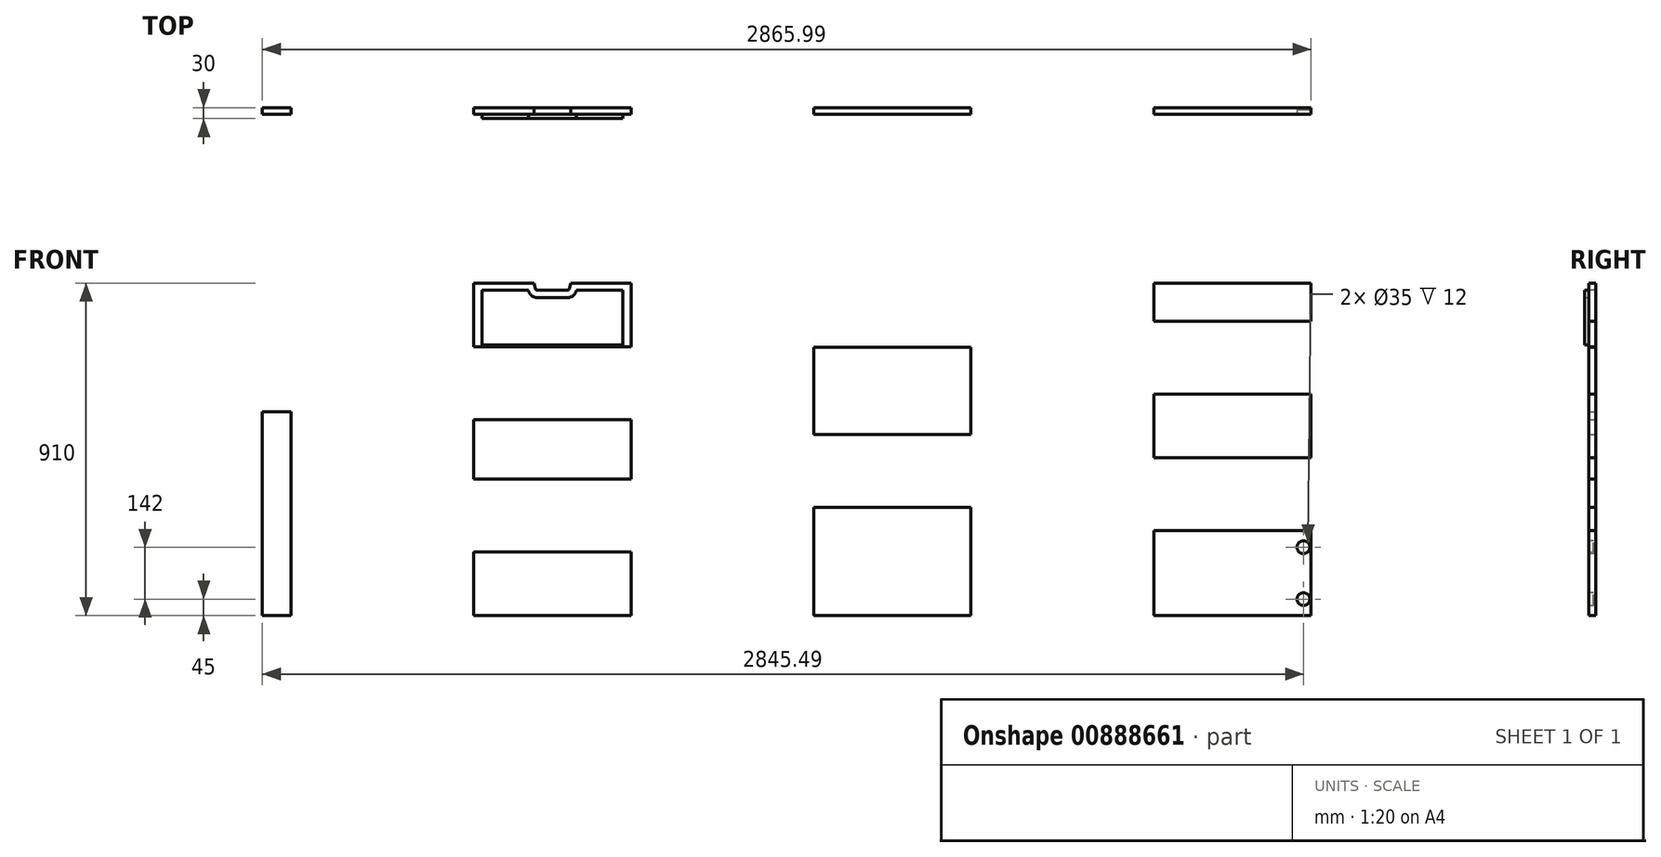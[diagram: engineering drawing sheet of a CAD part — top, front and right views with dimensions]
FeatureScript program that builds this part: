
annotation { "Feature Type Name" : "Feature", "Feature Type Description" : "" }
export const myFeature = defineFeature(function(context is Context, id is Id, definition is map)
    precondition{}
    {
        {
            assignVariable(context, id + "F0", {"name" : "ply", "anyValue" : 18});
        }
        {
            var Q0;
            Q0=qCreatedBy(makeId("Front.planeOp"),FACE);
            var sketch = newSketch(context, id + "F1", { "sketchPlane" : qUnion([Q0])});
            skLineSegment(sketch, "E0.bottom", {"start": v(0, 0) * mm, "end": v(429.33, 0) * mm});
            skLineSegment(sketch, "E0.top", {"start": v(0, 174) * mm, "end": v(429.33, 174) * mm});
            skLineSegment(sketch, "E0.left", {"start": v(0, 0) * mm, "end": v(0, 174) * mm});
            skLineSegment(sketch, "E0.right", {"start": v(429.33, 0) * mm, "end": v(429.33, 174) * mm});
            skLineSegment(sketch, "E1.bottom", {"start": v(0, -362) * mm, "end": v(429.33, -362) * mm});
            skLineSegment(sketch, "E1.top", {"start": v(0, -200) * mm, "end": v(429.33, -200) * mm});
            skLineSegment(sketch, "E1.left", {"start": v(0, -362) * mm, "end": v(0, -200) * mm});
            skLineSegment(sketch, "E1.right", {"start": v(429.33, -362) * mm, "end": v(429.33, -200) * mm});
            skLineSegment(sketch, "E2.bottom", {"start": v(0, -736) * mm, "end": v(429.33, -736) * mm});
            skLineSegment(sketch, "E2.top", {"start": v(0, -562) * mm, "end": v(429.33, -562) * mm});
            skLineSegment(sketch, "E2.left", {"start": v(0, -736) * mm, "end": v(0, -562) * mm});
            skLineSegment(sketch, "E2.right", {"start": v(429.33, -736) * mm, "end": v(429.33, -562) * mm});
            skLineSegment(sketch, "E3.bottom", {"start": v(-578, -736) * mm, "end": v(-500, -736) * mm});
            skLineSegment(sketch, "E3.top", {"start": v(-578, -178) * mm, "end": v(-500, -178) * mm});
            skLineSegment(sketch, "E3.left", {"start": v(-578, -736) * mm, "end": v(-578, -178) * mm});
            skLineSegment(sketch, "E3.right", {"start": v(-500, -736) * mm, "end": v(-500, -178) * mm});
            skLineSegment(sketch, "E4.bottom", {"start": v(929.33, -736) * mm, "end": v(1358.66, -736) * mm});
            skLineSegment(sketch, "E4.top", {"start": v(929.33, -440) * mm, "end": v(1358.66, -440) * mm});
            skLineSegment(sketch, "E4.left", {"start": v(929.33, -736) * mm, "end": v(929.33, -440) * mm});
            skLineSegment(sketch, "E4.right", {"start": v(1358.66, -736) * mm, "end": v(1358.66, -440) * mm});
            skLineSegment(sketch, "E5.bottom", {"start": v(929.33, -240) * mm, "end": v(1358.66, -240) * mm});
            skLineSegment(sketch, "E5.top", {"start": v(929.33, -2) * mm, "end": v(1358.66, -2) * mm});
            skLineSegment(sketch, "E5.left", {"start": v(929.33, -240) * mm, "end": v(929.33, -2) * mm});
            skLineSegment(sketch, "E5.right", {"start": v(1358.66, -240) * mm, "end": v(1358.66, -2) * mm});
            skLineSegment(sketch, "E6.bottom", {"start": v(1858.66, -736) * mm, "end": v(2287.99, -736) * mm});
            skLineSegment(sketch, "E6.top", {"start": v(1858.66, -504) * mm, "end": v(2287.99, -504) * mm});
            skLineSegment(sketch, "E6.left", {"start": v(1858.66, -736) * mm, "end": v(1858.66, -504) * mm});
            skLineSegment(sketch, "E6.right", {"start": v(2287.99, -736) * mm, "end": v(2287.99, -504) * mm});
            skLineSegment(sketch, "E7.bottom", {"start": v(1858.66, -304) * mm, "end": v(2287.99, -304) * mm});
            skLineSegment(sketch, "E7.top", {"start": v(1858.66, -130) * mm, "end": v(2287.99, -130) * mm});
            skLineSegment(sketch, "E7.left", {"start": v(1858.66, -304) * mm, "end": v(1858.66, -130) * mm});
            skLineSegment(sketch, "E7.right", {"start": v(2287.99, -304) * mm, "end": v(2287.99, -130) * mm});
            skLineSegment(sketch, "E8.bottom", {"start": v(1858.66, 70) * mm, "end": v(2287.99, 70) * mm});
            skLineSegment(sketch, "E8.top", {"start": v(1858.66, 174) * mm, "end": v(2287.99, 174) * mm});
            skLineSegment(sketch, "E8.left", {"start": v(1858.66, 70) * mm, "end": v(1858.66, 174) * mm});
            skLineSegment(sketch, "E8.right", {"start": v(2287.99, 70) * mm, "end": v(2287.99, 174) * mm});
            skSolve(sketch);
        }
        {
            var Q0;
            Q0=makeQuery(id+"F1.imprint","IMPRINT",FACE,{"disambiguationData":[TD([[makeQuery(id+"F1.imprint","IMPRINT",EDGE,{"derivedFrom":sQuery(id+"F1.wireOp",EDGE,"E3.bottom")}),1.0]])]});
            var Q1;
            Q1=makeQuery(id+"F1.imprint","IMPRINT",FACE,{"disambiguationData":[TD([[makeQuery(id+"F1.imprint","IMPRINT",EDGE,{"derivedFrom":sQuery(id+"F1.wireOp",EDGE,"E0.bottom")}),1.0]])]});
            var Q2;
            Q2=makeQuery(id+"F1.imprint","IMPRINT",FACE,{"disambiguationData":[TD([[makeQuery(id+"F1.imprint","IMPRINT",EDGE,{"derivedFrom":sQuery(id+"F1.wireOp",EDGE,"E1.bottom")}),1.0]])]});
            var Q3;
            Q3=makeQuery(id+"F1.imprint","IMPRINT",FACE,{"disambiguationData":[TD([[makeQuery(id+"F1.imprint","IMPRINT",EDGE,{"derivedFrom":sQuery(id+"F1.wireOp",EDGE,"E2.bottom")}),1.0]])]});
            var Q4;
            Q4=makeQuery(id+"F1.imprint","IMPRINT",FACE,{"disambiguationData":[TD([[makeQuery(id+"F1.imprint","IMPRINT",EDGE,{"derivedFrom":sQuery(id+"F1.wireOp",EDGE,"E5.bottom")}),1.0]])]});
            var Q5;
            Q5=makeQuery(id+"F1.imprint","IMPRINT",FACE,{"disambiguationData":[TD([[makeQuery(id+"F1.imprint","IMPRINT",EDGE,{"derivedFrom":sQuery(id+"F1.wireOp",EDGE,"E4.bottom")}),1.0]])]});
            var Q6;
            Q6=makeQuery(id+"F1.imprint","IMPRINT",FACE,{"disambiguationData":[TD([[makeQuery(id+"F1.imprint","IMPRINT",EDGE,{"derivedFrom":sQuery(id+"F1.wireOp",EDGE,"E8.bottom")}),1.0]])]});
            var Q7;
            Q7=makeQuery(id+"F1.imprint","IMPRINT",FACE,{"disambiguationData":[TD([[makeQuery(id+"F1.imprint","IMPRINT",EDGE,{"derivedFrom":sQuery(id+"F1.wireOp",EDGE,"E7.bottom")}),1.0]])]});
            var Q8;
            Q8=makeQuery(id+"F1.imprint","IMPRINT",FACE,{"disambiguationData":[TD([[makeQuery(id+"F1.imprint","IMPRINT",EDGE,{"derivedFrom":sQuery(id+"F1.wireOp",EDGE,"E6.bottom")}),1.0]])]});
            extrude(context, id + "F2", {"entities" : qUnion([Q0, Q1, Q2, Q3, Q4, Q5, Q6, Q7, Q8]), "depth" : (getVariable(context, 'ply')) * mm, "offsetDistance" : 25 * mm});
        }
        {
            var Q0;
            Q0=makeQuery(id+"F2.opExtrude","CAP_FACE",FACE,{"disambiguationData":[OSD([sQuery(id+"F1.wireOp",EDGE,"E6.bottom"),sQuery(id+"F1.wireOp",EDGE,"E6.top"),sQuery(id+"F1.wireOp",EDGE,"E6.left"),sQuery(id+"F1.wireOp",EDGE,"E6.right")])],"isStart":false});
            var sketch = newSketch(context, id + "F3", { "sketchPlane" : qUnion([Q0])});
            skCircle(sketch, "E9", {"center": v(2267.49, -549) * mm, "radius": 17.5 * mm});
            skLineSegment(sketch, "E10", {"start": v(1858.66, -620) * mm, "end": v(2287.99, -620) * mm, "construction": true});
            skCircle(sketch, "E11.MirrorC", {"center": v(2267.49, -691) * mm, "radius": 17.5 * mm});
            skSolve(sketch);
        }
        {
            var Q0;
            Q0 = qSketchRegion(id + "F3", true);
            extrude(context, id + "F4", {"entities" : qUnion([Q0]), "operationType" : NewBodyOperationType.REMOVE, "oppositeDirection" : true, "depth" : 12 * mm, "offsetDistance" : 25 * mm});
        }
        {
            var Q0;
            Q0=makeQuery(id+"F2.opExtrude","CAP_FACE",FACE,{"disambiguationData":[OSD([sQuery(id+"F1.wireOp",EDGE,"E0.bottom"),sQuery(id+"F1.wireOp",EDGE,"E0.top"),sQuery(id+"F1.wireOp",EDGE,"E0.left"),sQuery(id+"F1.wireOp",EDGE,"E0.right")])],"isStart":false});
            var sketch = newSketch(context, id + "F5", { "sketchPlane" : qUnion([Q0])});
            skLineSegment(sketch, "E12", {"start": v(214.66, 174) * mm, "end": v(214.66, 0) * mm, "construction": true});
            skLineSegment(sketch, "E13.0", {"start": v(173.5, 154) * mm, "end": v(214.66, 154) * mm});
            skLineSegment(sketch, "E14", {"start": v(168.67, 157.7) * mm, "end": v(164.3, 174) * mm});
            skPoint(sketch, "E15.visualSharp", {"position": v(169.67, 154) * mm});
            skArc(sketch, "E15.filletArc", {"start": v(168.67, 157.7) * mm, "mid": v(170.46, 155.03) * mm, "end": v(173.5, 154) * mm});
            skArc(sketch, "E16.MirrorCS", {"start": v(260.66, 157.7) * mm, "mid": v(258.87, 155.03) * mm, "end": v(255.83, 154) * mm});
            skLineSegment(sketch, "E17.MirrorCS", {"start": v(255.83, 154) * mm, "end": v(214.66, 154) * mm});
            skLineSegment(sketch, "E18.MirrorCS", {"start": v(260.66, 157.7) * mm, "end": v(265.02, 174) * mm});
            skSolve(sketch);
        }
        {
            var Q0;
            Q0=makeQuery(id+"F5.imprint","IMPRINT",FACE,{"disambiguationData":[TD([[makeQuery(id+"F5.imprint","IMPRINT",EDGE,{"derivedFrom":sQuery(id+"F5.wireOp",EDGE,"E13.0")}),1.0]])]});
            var Q1;
            Q1=makeQuery(id+"F5.imprint","IMPRINT",FACE,{"disambiguationData":[TD([[makeQuery(id+"F5.imprint","IMPRINT",EDGE,{"derivedFrom":sQuery(id+"F5.wireOp",EDGE,"f27caa91-3240-40d5-94f7-d264efe6a361.0")}),1.0]])]});
            extrude(context, id + "F6", {"entities" : qUnion([Q0, Q1]), "operationType" : NewBodyOperationType.REMOVE, "oppositeDirection" : true, "depth" : (getVariable(context, 'ply')) * mm, "offsetDistance" : 25 * mm});
        }
        {
            var Q0;
            Q0=makeQuery(id+"F2.opExtrude","CAP_FACE",FACE,{"disambiguationData":[OSD([sQuery(id+"F1.wireOp",EDGE,"E0.bottom"),sQuery(id+"F1.wireOp",EDGE,"E0.top"),sQuery(id+"F1.wireOp",EDGE,"E0.left"),sQuery(id+"F1.wireOp",EDGE,"E0.right")])],"isStart":false});
            var sketch = newSketch(context, id + "F7", { "sketchPlane" : qUnion([Q0])});
            skLineSegment(sketch, "E19.0", {"start": v(22, 5) * mm, "end": v(22, 154) * mm});
            skLineSegment(sketch, "E20.0", {"start": v(407.33, 5) * mm, "end": v(407.33, 154) * mm});
            skLineSegment(sketch, "E21.9", {"start": v(22, 5) * mm, "end": v(407.33, 5) * mm});
            skLineSegment(sketch, "E22.0", {"start": v(255.83, 134) * mm, "end": v(173.5, 134) * mm});
            skArc(sketch, "E22.1", {"start": v(279.98, 152.53) * mm, "mid": v(271.05, 139.17) * mm, "end": v(255.83, 134) * mm});
            skArc(sketch, "E22.2", {"start": v(173.5, 134) * mm, "mid": v(158.28, 139.17) * mm, "end": v(149.35, 152.53) * mm});
            skLineSegment(sketch, "E22.3", {"start": v(280.37, 154) * mm, "end": v(279.98, 152.53) * mm});
            skLineSegment(sketch, "E22.4", {"start": v(407.33, 154) * mm, "end": v(280.37, 154) * mm});
            skLineSegment(sketch, "E22.6", {"start": v(149.35, 152.53) * mm, "end": v(148.96, 154) * mm});
            skLineSegment(sketch, "E22.7", {"start": v(148.96, 154) * mm, "end": v(22, 154) * mm});
            skSolve(sketch);
        }
        {
            var Q0;
            Q0=makeQuery(id+"F7.imprint","IMPRINT",FACE,{"disambiguationData":[TD([[makeQuery(id+"F7.imprint","IMPRINT",EDGE,{"derivedFrom":sQuery(id+"F7.wireOp",EDGE,"E19.0")}),-1.0]])]});
            extrude(context, id + "F8", {"entities" : qUnion([Q0]), "depth" : 12 * mm, "offsetDistance" : 25 * mm});
        }
    });
